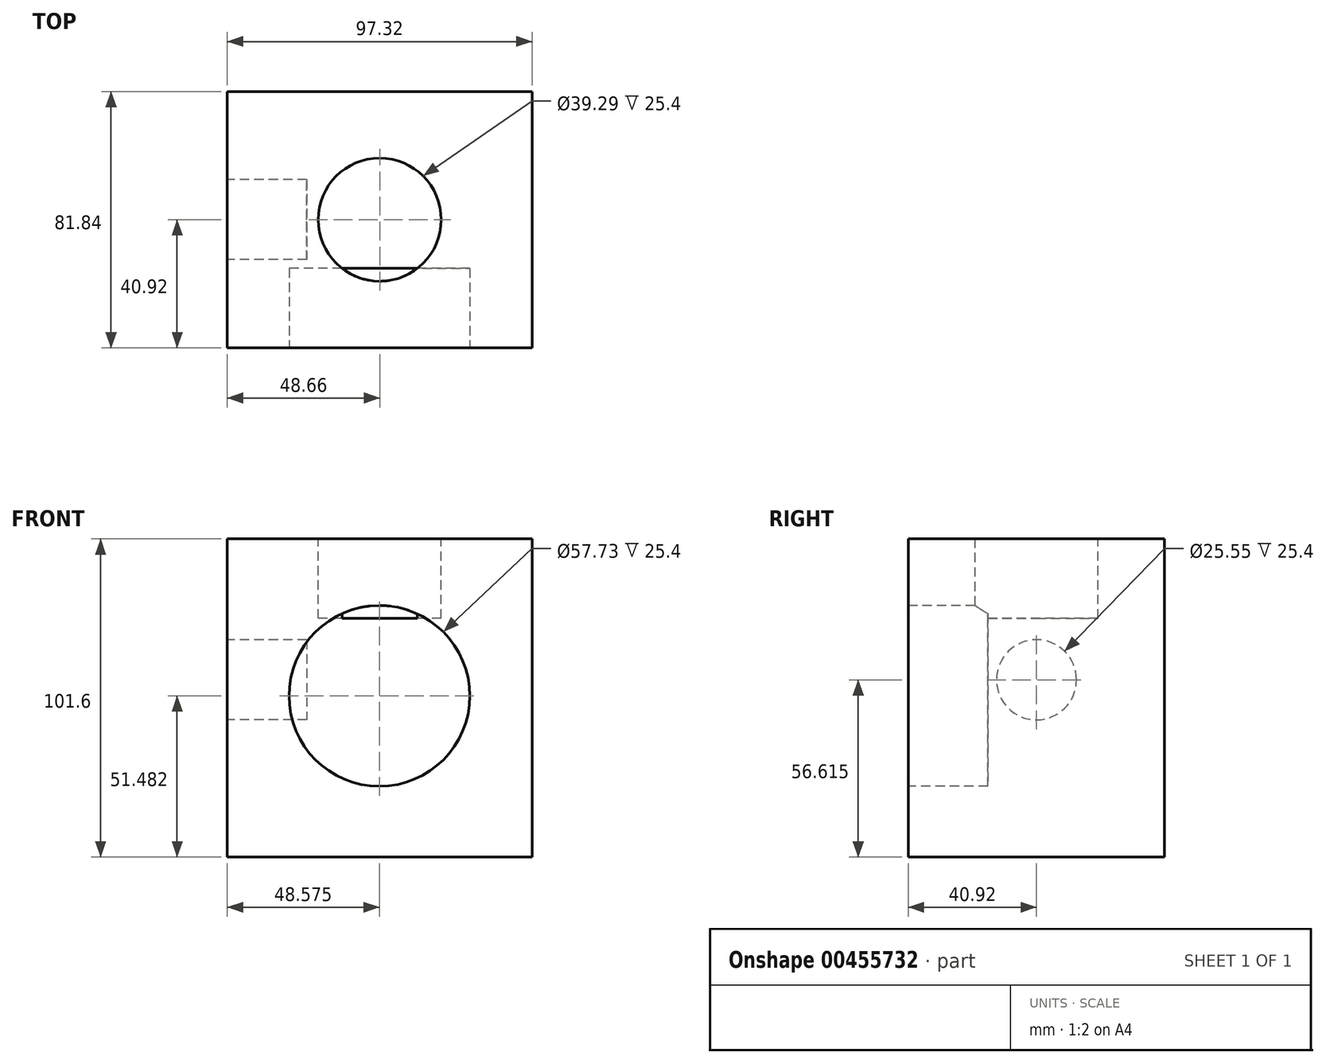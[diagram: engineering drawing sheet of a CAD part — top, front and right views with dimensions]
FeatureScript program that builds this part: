
annotation { "Feature Type Name" : "Feature", "Feature Type Description" : "" }
export const myFeature = defineFeature(function(context is Context, id is Id, definition is map)
    precondition{}
    {
        {
            var Q0;
            Q0=qCreatedBy(makeId("Top.planeOp"),FACE);
            var sketch = newSketch(context, id + "F0", { "sketchPlane" : qUnion([Q0])});
            skLineSegment(sketch, "E0.bottom", {"start": v(48.66, -40.92) * mm, "end": v(-48.66, -40.92) * mm});
            skLineSegment(sketch, "E0.top", {"start": v(48.66, 40.92) * mm, "end": v(-48.66, 40.92) * mm});
            skLineSegment(sketch, "E0.left", {"start": v(48.66, -40.92) * mm, "end": v(48.66, 40.92) * mm});
            skLineSegment(sketch, "E0.right", {"start": v(-48.66, -40.92) * mm, "end": v(-48.66, 40.92) * mm});
            skPoint(sketch, "E0.middle", {"position": v(0, 0) * mm});
            skSolve(sketch);
        }
        {
            var Q0;
            Q0 = qSketchRegion(id + "F0", true);
            var Q1;
            Q1=makeQuery(id+"F0.imprint","IMPRINT",FACE,{"disambiguationData":[TD([[makeQuery(id+"F0.imprint","IMPRINT",EDGE,{"derivedFrom":sQuery(id+"F0.wireOp",EDGE,"E0.bottom")}),-1.0]])]});
            extrude(context, id + "F1", {"entities" : qUnion([Q0, Q1]), "depth" : 101.6 * mm});
        }
        {
            var Q0;
            Q0=makeQuery(id+"F1.opExtrude","CAP_FACE",FACE,{"disambiguationData":[OSD([sQuery(id+"F0.wireOp",EDGE,"E0.bottom"),sQuery(id+"F0.wireOp",EDGE,"E0.top"),sQuery(id+"F0.wireOp",EDGE,"E0.left"),sQuery(id+"F0.wireOp",EDGE,"E0.right")])],"isStart":false});
            var sketch = newSketch(context, id + "F2", { "sketchPlane" : qUnion([Q0])});
            skCircle(sketch, "E1", {"center": v(0, 0) * mm, "radius": 19.64 * mm});
            skSolve(sketch);
        }
        {
            var Q0;
            Q0=makeQuery(id+"F2.imprint","IMPRINT",FACE,{"disambiguationData":[TD([[makeQuery(id+"F2.imprint","IMPRINT",EDGE,{"derivedFrom":sQuery(id+"F2.wireOp",EDGE,"E1")}),1.0]])]});
            extrude(context, id + "F3", {"entities" : qUnion([Q0]), "operationType" : NewBodyOperationType.REMOVE, "oppositeDirection" : true, "depth" : 25.4 * mm});
        }
        {
            var Q0;
            Q0=makeQuery(id+"F1.opExtrude","SWEPT_FACE",FACE,{"disambiguationData":[OSD([sQuery(id+"F0.wireOp",EDGE,"E0.bottom")])]});
            var sketch = newSketch(context, id + "F4", { "sketchPlane" : qUnion([Q0])});
            skCircle(sketch, "E2", {"center": v(-0.08, 51.48) * mm, "radius": 28.87 * mm});
            skSolve(sketch);
        }
        {
            var Q0;
            Q0=makeQuery(id+"F1.opExtrude","SWEPT_FACE",FACE,{"disambiguationData":[OSD([sQuery(id+"F0.wireOp",EDGE,"E0.right")])]});
            var sketch = newSketch(context, id + "F5", { "sketchPlane" : qUnion([Q0])});
            skCircle(sketch, "E3", {"center": v(0, 56.62) * mm, "radius": 12.78 * mm});
            skSolve(sketch);
        }
        {
            var Q0;
            Q0=makeQuery(id+"F5.imprint","IMPRINT",FACE,{"disambiguationData":[TD([[makeQuery(id+"F5.imprint","IMPRINT",EDGE,{"derivedFrom":sQuery(id+"F5.wireOp",EDGE,"E3")}),1.0]])]});
            extrude(context, id + "F6", {"entities" : qUnion([Q0]), "operationType" : NewBodyOperationType.REMOVE, "oppositeDirection" : true, "depth" : 25.4 * mm});
        }
        {
            var Q0;
            Q0=makeQuery(id+"F4.imprint","IMPRINT",FACE,{"disambiguationData":[TD([[makeQuery(id+"F4.imprint","IMPRINT",EDGE,{"derivedFrom":sQuery(id+"F4.wireOp",EDGE,"E2")}),1.0]])]});
            var Q1;
            Q1=sQuery(id+"F4.wireOp",EDGE,"E2");
            extrude(context, id + "F7", {"entities" : qUnion([Q0]), "operationType" : NewBodyOperationType.REMOVE, "surfaceEntities" : qUnion([Q1]), "oppositeDirection" : true, "depth" : 25.4 * mm});
        }
    });
